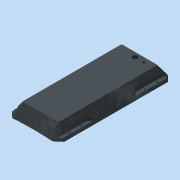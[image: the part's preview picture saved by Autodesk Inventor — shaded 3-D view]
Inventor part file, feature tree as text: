
AUTODESK INVENTOR PART (.ipt)
format: ipt  version: 2015 (Build 190159000, 159)  size: 490,496 bytes
history: native  units: in
note: dims shown in document units (in); Inventor stores cm internally (conversion verified against a paired STEP export)
features: sketch x14, extrude x13, projected_geometry x9, plane x5, fillet x5, loft x1, mirror x1
ambient origin geometry x8: Origin, YZ Plane, XZ Plane, XY Plane, X Axis, Y Axis, Z Axis, Center Point
bodies: Body1 (feature_tree)
feature tree (48):
  sketch  "Sketch1"  dims[d0=45.0deg d1=12.1574in]
  sketch  "Sketch5"  dims[d6=1.0in d7=1.0in]
  plane  "Work Plane1"
  loft  "Loft2"
  plane  "Work Plane2"
  extrude  "Extrusion1"  Depth=1.0in
  extrude  "Extrusion3"  Depth=1.0in
  plane  "Work Plane3"
  extrude  "Extrusion2"  Depth=1.0in
  plane  "Work Plane5"
  extrude  "Extrusion4"  Depth=0.125in
  extrude  "Extrusion5"  Depth=0.125in
  extrude  "Extrusion6"  Depth=0.125in
  extrude  "Extrusion7"  Depth=0.125in
  mirror  "Mirror1"
  extrude  "Extrusion8"  TaperAngle=0.0deg  [1 undecoded]
  extrude  "Extrusion10"  Depth=1.0in TaperAngle=0.0deg
  fillet  "Fillet1"  Radius=8.3074in
  extrude  "Extrusion11"  Depth=0.125in TaperAngle=0.0deg
  extrude  "Extrusion12"  Depth=0.125in TaperAngle=0.0deg
  fillet  "Fillet3"  Radius=0.1875in
  extrude  "Extrusion13"  Depth=0.125in TaperAngle=0.0deg
  fillet  "Fillet4"  Radius=0.201in
  extrude  "Extrusion14"  Depth=1.5in
  fillet  "Fillet5"  Radius=0.125in
  fillet  "Fillet6"  Radius=0.0825in
  sketch  "Sketch3"  dims[d2=4.4in d3=1.0in]
  sketch  "Sketch4"  dims[d4=1.0in d5=1.0in]
  plane  "Work Plane4"
  sketch  "Sketch6"  dims[d21=0.125in d22=0.125in]
  sketch  "Sketch7"  dims[d23=0.125in d24=0.125in]
  sketch  "Sketch8"  dims[d25=0.125in d26=0.125in]
  sketch  "Sketch9"  dims[d27=0.125in d28=0.125in]
  projected_geometry  "Projected Loop1"
  sketch  "Sketch10"  dims[d29=0.0in d30=90.0deg d31=0.0in d32=90.0deg]
  projected_geometry  "Projected Loop2"
  sketch  "Sketch12"  dims[d33=-0.3125in d34=1.0in d35=0.0in d36=8.3074in]
  sketch  "Sketch13"  dims[d37=0.1875in d38=0.125in d39=0.0in]
  sketch  "Sketch14"  dims[d41=1.362in d42=0.125in d43=0.0in d44=0.1875in]
  sketch  "Sketch15"  dims[d45=0.375in d47=0.125in d48=0.0in d49=0.201in]
  sketch  "Sketch16"  dims[d50=0.201in d51=1.5in d52=0.125in d53=0.0in d54=0.0825in d55=0.125in d56=0.0in d57=0.75in d58=0.0704in d59=1.0in d60=0.5in d61=0.1575in d62=0.1181in d63=0.0591in d64=0.0in d65=0.1875in d66=0.0in d69=1.0in d70=0.625in d71=0.125in d72=0.0in d73=0.125in d76=0.125in d77=0.0in d78=0.3189in d79=0.5512in d80=0.0133in d81=0.0in d82=0.0394in d83=1.0in d84=0.0054in d85=0.0in d86=0.0787in d87=0.3in d88=0.375in d89=0.0in d90=0.5in d91=0.0in d92=61.729in d93=0.0625in d94=0.0625in]
  projected_geometry  "Projected Loop3"
  projected_geometry  "Project Cut Edges1"
  projected_geometry  "Project Cut Edges2"
  projected_geometry  "Project Cut Edges3"
  projected_geometry  "Project Cut Edges5"
  projected_geometry  "Project Cut Edges6"
  projected_geometry  "Project Cut Edges7"
note: 1 required parameter value undecoded (feature->parameter linkage not recoverable at this tier; creation-order binding heuristic only, values carry confidence <= 0.55)
